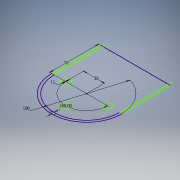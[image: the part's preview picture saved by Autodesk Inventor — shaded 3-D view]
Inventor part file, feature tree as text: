
AUTODESK INVENTOR PART (.ipt)
format: ipt  version: 2019 (Build 230136000, 136)  size: 95,232 bytes
history: native  units: mm
features: sketch x1
ambient origin geometry x8: Origin, YZ Plane, XZ Plane, XY Plane, X Axis, Y Axis, Z Axis, Center Point
feature tree (1):
  sketch  "Sketch1"  dims[d0=100.0mm d1=11.0mm d2=30.0mm d3=30.0mm d5=180.0deg d7=3.5mm d8=70.0mm]
